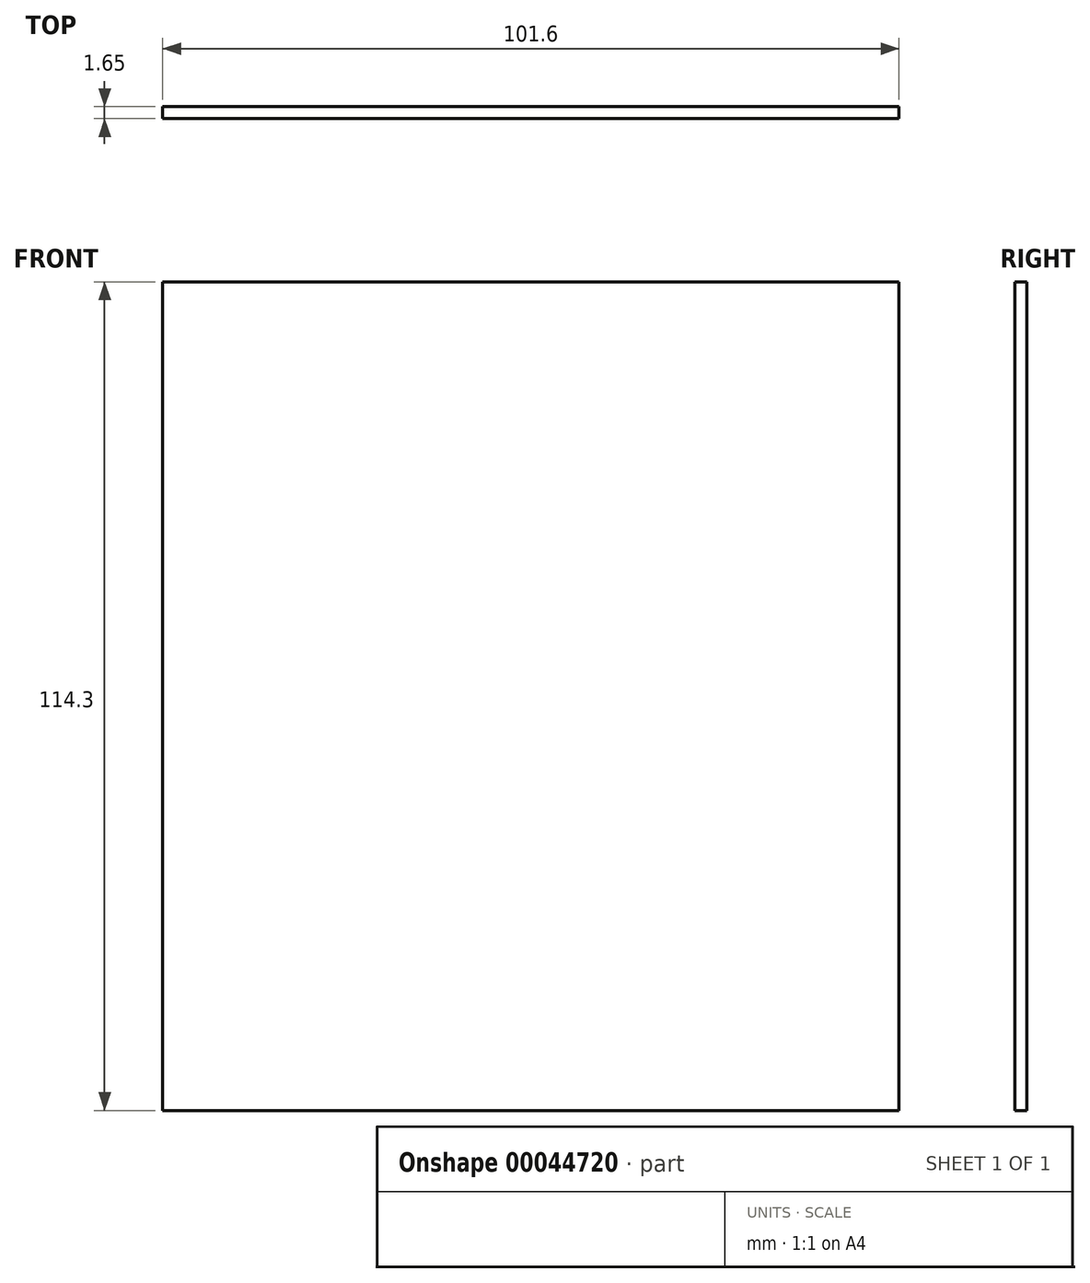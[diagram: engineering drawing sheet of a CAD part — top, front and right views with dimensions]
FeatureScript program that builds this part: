
annotation { "Feature Type Name" : "Feature", "Feature Type Description" : "" }
export const myFeature = defineFeature(function(context is Context, id is Id, definition is map)
    precondition{}
    {
        {
            var Q0;
            Q0=qCreatedBy(makeId("Front.planeOp"),FACE);
            var sketch = newSketch(context, id + "F0", { "sketchPlane" : qUnion([Q0])});
            skLineSegment(sketch, "E0.bottom", {"start": v(-46.55, 20.06) * mm, "end": v(55.05, 20.06) * mm});
            skLineSegment(sketch, "E0.top", {"start": v(-46.55, -94.24) * mm, "end": v(55.05, -94.24) * mm});
            skLineSegment(sketch, "E0.left", {"start": v(-46.55, 20.06) * mm, "end": v(-46.55, -94.24) * mm});
            skLineSegment(sketch, "E0.right", {"start": v(55.05, 20.06) * mm, "end": v(55.05, -94.24) * mm});
            skSolve(sketch);
        }
        {
            var Q0;
            Q0=makeQuery(id+"F0.imprint","IMPRINT",FACE,{"disambiguationData":[TD([[makeQuery(id+"F0.imprint","IMPRINT",EDGE,{"derivedFrom":sQuery(id+"F0.wireOp",EDGE,"E0.bottom")}),-1.0]])]});
            extrude(context, id + "F1", {"entities" : qUnion([Q0]), "oppositeDirection" : true, "depth" : 1.65 * mm});
        }
    });
